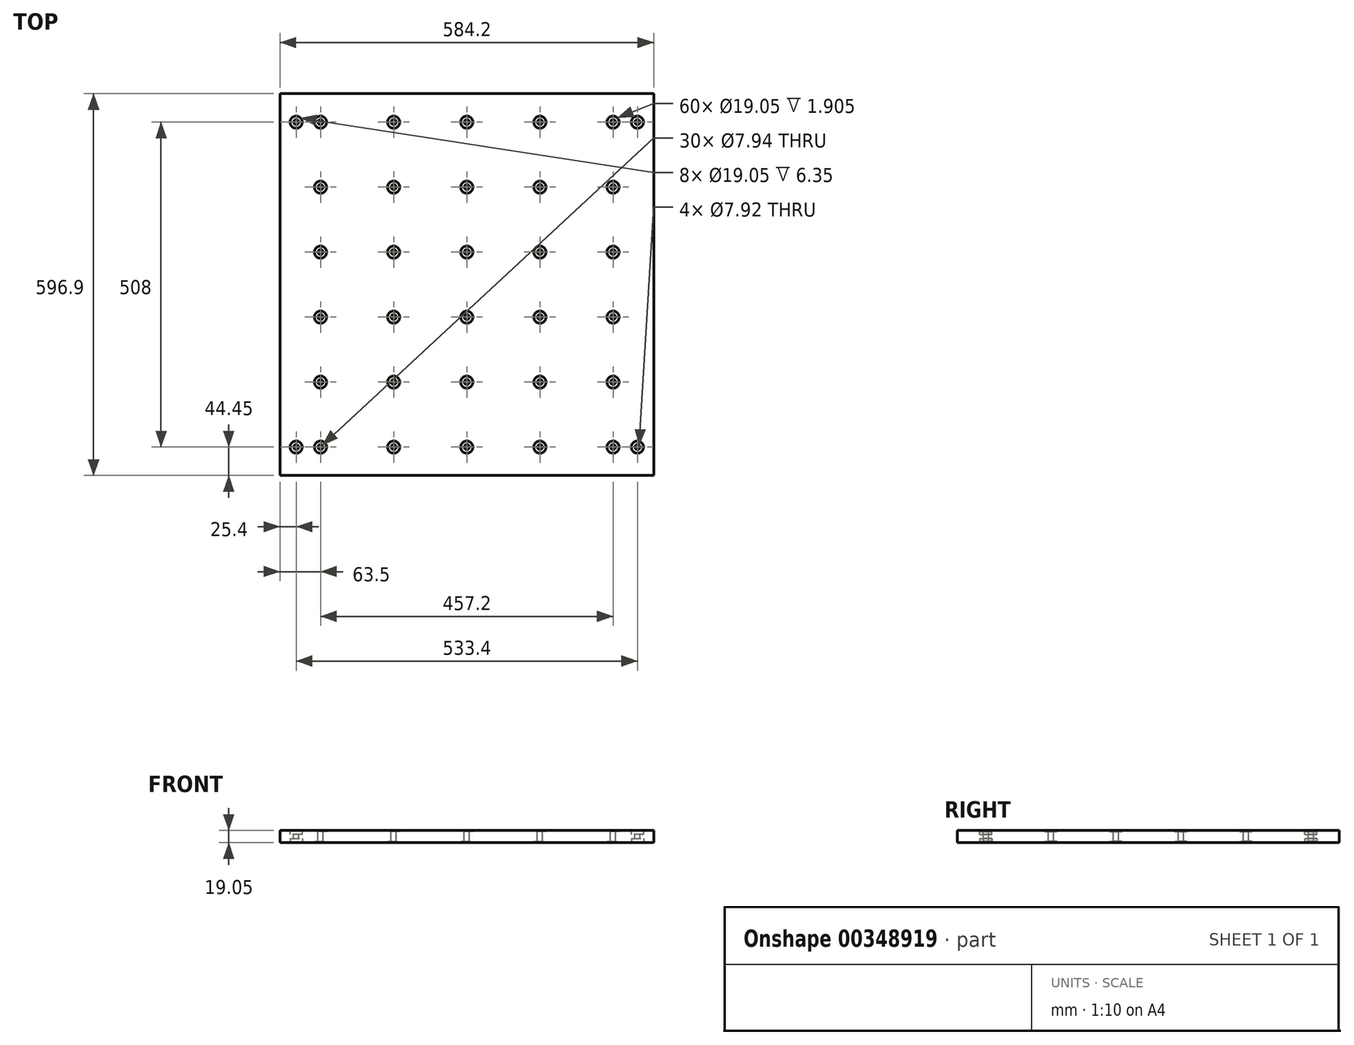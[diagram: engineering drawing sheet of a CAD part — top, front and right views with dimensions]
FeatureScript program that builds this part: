
annotation { "Feature Type Name" : "Feature", "Feature Type Description" : "" }
export const myFeature = defineFeature(function(context is Context, id is Id, definition is map)
    precondition{}
    {
        {
            var Q0;
            Q0=qCreatedBy(makeId("Top.planeOp"),FACE);
            var sketch = newSketch(context, id + "F0", { "sketchPlane" : qUnion([Q0])});
            skLineSegment(sketch, "E0.bottom", {"start": v(0, 0) * mm, "end": v(584.2, 0) * mm});
            skLineSegment(sketch, "E0.top", {"start": v(0, -596.9) * mm, "end": v(584.2, -596.9) * mm});
            skLineSegment(sketch, "E0.left", {"start": v(0, 0) * mm, "end": v(0, -596.9) * mm});
            skLineSegment(sketch, "E0.right", {"start": v(584.2, 0) * mm, "end": v(584.2, -596.9) * mm});
            skSolve(sketch);
        }
        {
            var Q0;
            Q0=qSketchRegion(id+"F0",true);
            extrude(context, id + "F1", {"entities" : qUnion([Q0]), "depth" : 19.05 * mm});
        }
        {
            var Q0;
            Q0=makeQuery(id+"F1.opExtrude","CAP_FACE",FACE,{"disambiguationData":[OSD([sQuery(id+"F0.wireOp",EDGE,"E0.bottom"),sQuery(id+"F0.wireOp",EDGE,"E0.top"),sQuery(id+"F0.wireOp",EDGE,"E0.left"),sQuery(id+"F0.wireOp",EDGE,"E0.right")])],"isStart":false});
            var sketch = newSketch(context, id + "F2", { "sketchPlane" : qUnion([Q0])});
            skCircle(sketch, "E1", {"center": v(25.4, -552.45) * mm, "radius": 9.53 * mm});
            skCircle(sketch, "E2.0.1.0", {"center": v(25.4, -44.45) * mm, "radius": 9.53 * mm});
            skCircle(sketch, "E2.1.0.0", {"center": v(558.8, -552.45) * mm, "radius": 9.53 * mm});
            skCircle(sketch, "E2.1.1.0", {"center": v(558.8, -44.45) * mm, "radius": 9.53 * mm});
            skLineSegment(sketch, "E2.direction1", {"start": v(25.4, -552.45) * mm, "end": v(558.8, -552.45) * mm, "construction": true});
            skLineSegment(sketch, "E2.direction2", {"start": v(25.4, -552.45) * mm, "end": v(25.4, -44.45) * mm, "construction": true});
            skSolve(sketch);
        }
        {
            var Q0;
            Q0=qSketchRegion(id+"F2",true);
            extrude(context, id + "F3", {"entities" : qUnion([Q0]), "operationType" : NewBodyOperationType.REMOVE, "oppositeDirection" : true, "depth" : 6.35 * mm});
        }
        {
            var Q0;
            Q0=makeQuery(id+"F1.opExtrude","CAP_FACE",FACE,{"disambiguationData":[OSD([sQuery(id+"F0.wireOp",EDGE,"E0.bottom"),sQuery(id+"F0.wireOp",EDGE,"E0.top"),sQuery(id+"F0.wireOp",EDGE,"E0.left"),sQuery(id+"F0.wireOp",EDGE,"E0.right")])],"isStart":false});
            var sketch = newSketch(context, id + "F4", { "sketchPlane" : qUnion([Q0])});
            skCircle(sketch, "E3", {"center": v(25.4, -552.45) * mm, "radius": 3.96 * mm});
            skCircle(sketch, "E4.0.1.0", {"center": v(25.4, -44.45) * mm, "radius": 3.96 * mm});
            skCircle(sketch, "E4.1.0.0", {"center": v(558.8, -552.45) * mm, "radius": 3.96 * mm});
            skCircle(sketch, "E4.1.1.0", {"center": v(558.8, -44.45) * mm, "radius": 3.96 * mm});
            skLineSegment(sketch, "E4.direction1", {"start": v(25.4, -552.45) * mm, "end": v(558.8, -552.45) * mm, "construction": true});
            skLineSegment(sketch, "E4.direction2", {"start": v(25.4, -552.45) * mm, "end": v(25.4, -44.45) * mm, "construction": true});
            skSolve(sketch);
        }
        {
            var Q0;
            Q0=qSketchRegion(id+"F4",true);
            extrude(context, id + "F5", {"entities" : qUnion([Q0]), "operationType" : NewBodyOperationType.REMOVE, "endBound" : BoundingType.THROUGH_ALL, "oppositeDirection" : true, "depth" : 25.4 * mm});
        }
        {
            var Q0;
            Q0=makeQuery(id+"F1.opExtrude","CAP_FACE",FACE,{"disambiguationData":[OSD([sQuery(id+"F0.wireOp",EDGE,"E0.bottom"),sQuery(id+"F0.wireOp",EDGE,"E0.top"),sQuery(id+"F0.wireOp",EDGE,"E0.left"),sQuery(id+"F0.wireOp",EDGE,"E0.right")])],"isStart":true});
            var sketch = newSketch(context, id + "F6", { "sketchPlane" : qUnion([Q0])});
            skCircle(sketch, "E5", {"center": v(25.4, 44.45) * mm, "radius": 9.53 * mm});
            skCircle(sketch, "E6.0.1.0", {"center": v(25.4, 552.45) * mm, "radius": 9.53 * mm});
            skCircle(sketch, "E6.1.0.0", {"center": v(558.8, 44.45) * mm, "radius": 9.53 * mm});
            skCircle(sketch, "E6.1.1.0", {"center": v(558.8, 552.45) * mm, "radius": 9.53 * mm});
            skLineSegment(sketch, "E6.direction1", {"start": v(25.4, 44.45) * mm, "end": v(558.8, 44.45) * mm, "construction": true});
            skLineSegment(sketch, "E6.direction2", {"start": v(25.4, 44.45) * mm, "end": v(25.4, 552.45) * mm, "construction": true});
            skSolve(sketch);
        }
        {
            var Q0;
            Q0=qSketchRegion(id+"F6",true);
            extrude(context, id + "F7", {"entities" : qUnion([Q0]), "operationType" : NewBodyOperationType.REMOVE, "oppositeDirection" : true, "depth" : 6.35 * mm});
        }
        {
            var Q0;
            Q0=makeQuery(id+"F1.opExtrude","CAP_FACE",FACE,{"disambiguationData":[OSD([sQuery(id+"F0.wireOp",EDGE,"E0.bottom"),sQuery(id+"F0.wireOp",EDGE,"E0.top"),sQuery(id+"F0.wireOp",EDGE,"E0.left"),sQuery(id+"F0.wireOp",EDGE,"E0.right")])],"isStart":false});
            var sketch = newSketch(context, id + "F8", { "sketchPlane" : qUnion([Q0])});
            skCircle(sketch, "E7", {"center": v(63.5, -552.45) * mm, "radius": 9.53 * mm});
            skCircle(sketch, "E8.0.1.0", {"center": v(63.5, -450.85) * mm, "radius": 9.53 * mm});
            skCircle(sketch, "E8.0.2.0", {"center": v(63.5, -349.25) * mm, "radius": 9.53 * mm});
            skCircle(sketch, "E8.0.3.0", {"center": v(63.5, -247.65) * mm, "radius": 9.53 * mm});
            skCircle(sketch, "E8.0.4.0", {"center": v(63.5, -146.05) * mm, "radius": 9.53 * mm});
            skCircle(sketch, "E8.0.5.0", {"center": v(63.5, -44.45) * mm, "radius": 9.53 * mm});
            skCircle(sketch, "E8.1.0.0", {"center": v(177.8, -552.45) * mm, "radius": 9.53 * mm});
            skCircle(sketch, "E8.1.1.0", {"center": v(177.8, -450.85) * mm, "radius": 9.53 * mm});
            skCircle(sketch, "E8.1.2.0", {"center": v(177.8, -349.25) * mm, "radius": 9.53 * mm});
            skCircle(sketch, "E8.1.3.0", {"center": v(177.8, -247.65) * mm, "radius": 9.53 * mm});
            skCircle(sketch, "E8.1.4.0", {"center": v(177.8, -146.05) * mm, "radius": 9.53 * mm});
            skCircle(sketch, "E8.1.5.0", {"center": v(177.8, -44.45) * mm, "radius": 9.53 * mm});
            skCircle(sketch, "E8.2.0.0", {"center": v(292.1, -552.45) * mm, "radius": 9.53 * mm});
            skCircle(sketch, "E8.2.1.0", {"center": v(292.1, -450.85) * mm, "radius": 9.53 * mm});
            skCircle(sketch, "E8.2.2.0", {"center": v(292.1, -349.25) * mm, "radius": 9.53 * mm});
            skCircle(sketch, "E8.2.3.0", {"center": v(292.1, -247.65) * mm, "radius": 9.53 * mm});
            skCircle(sketch, "E8.2.4.0", {"center": v(292.1, -146.05) * mm, "radius": 9.53 * mm});
            skCircle(sketch, "E8.2.5.0", {"center": v(292.1, -44.45) * mm, "radius": 9.53 * mm});
            skCircle(sketch, "E8.3.0.0", {"center": v(406.4, -552.45) * mm, "radius": 9.53 * mm});
            skCircle(sketch, "E8.3.1.0", {"center": v(406.4, -450.85) * mm, "radius": 9.53 * mm});
            skCircle(sketch, "E8.3.2.0", {"center": v(406.4, -349.25) * mm, "radius": 9.53 * mm});
            skCircle(sketch, "E8.3.3.0", {"center": v(406.4, -247.65) * mm, "radius": 9.53 * mm});
            skCircle(sketch, "E8.3.4.0", {"center": v(406.4, -146.05) * mm, "radius": 9.53 * mm});
            skCircle(sketch, "E8.3.5.0", {"center": v(406.4, -44.45) * mm, "radius": 9.53 * mm});
            skCircle(sketch, "E8.4.0.0", {"center": v(520.7, -552.45) * mm, "radius": 9.53 * mm});
            skCircle(sketch, "E8.4.1.0", {"center": v(520.7, -450.85) * mm, "radius": 9.53 * mm});
            skCircle(sketch, "E8.4.2.0", {"center": v(520.7, -349.25) * mm, "radius": 9.53 * mm});
            skCircle(sketch, "E8.4.3.0", {"center": v(520.7, -247.65) * mm, "radius": 9.53 * mm});
            skCircle(sketch, "E8.4.4.0", {"center": v(520.7, -146.05) * mm, "radius": 9.53 * mm});
            skCircle(sketch, "E8.4.5.0", {"center": v(520.7, -44.45) * mm, "radius": 9.53 * mm});
            skLineSegment(sketch, "E8.direction1", {"start": v(63.5, -552.45) * mm, "end": v(177.8, -552.45) * mm, "construction": true});
            skLineSegment(sketch, "E8.direction2", {"start": v(63.5, -552.45) * mm, "end": v(63.5, -450.85) * mm, "construction": true});
            skSolve(sketch);
        }
        {
            var Q0;
            Q0=qSketchRegion(id+"F8",true);
            extrude(context, id + "F9", {"entities" : qUnion([Q0]), "operationType" : NewBodyOperationType.REMOVE, "oppositeDirection" : true, "depth" : 1.9 * mm});
        }
        {
            var Q0;
            Q0=makeQuery(id+"F1.opExtrude","CAP_FACE",FACE,{"disambiguationData":[OSD([sQuery(id+"F0.wireOp",EDGE,"E0.bottom"),sQuery(id+"F0.wireOp",EDGE,"E0.top"),sQuery(id+"F0.wireOp",EDGE,"E0.left"),sQuery(id+"F0.wireOp",EDGE,"E0.right")])],"isStart":false});
            var sketch = newSketch(context, id + "F10", { "sketchPlane" : qUnion([Q0])});
            skCircle(sketch, "E9", {"center": v(63.5, -552.45) * mm, "radius": 3.97 * mm});
            skCircle(sketch, "E10.0.1.0", {"center": v(63.5, -450.85) * mm, "radius": 3.97 * mm});
            skCircle(sketch, "E10.0.2.0", {"center": v(63.5, -349.25) * mm, "radius": 3.97 * mm});
            skCircle(sketch, "E10.0.3.0", {"center": v(63.5, -247.65) * mm, "radius": 3.97 * mm});
            skCircle(sketch, "E10.0.4.0", {"center": v(63.5, -146.05) * mm, "radius": 3.97 * mm});
            skCircle(sketch, "E10.0.5.0", {"center": v(63.5, -44.45) * mm, "radius": 3.97 * mm});
            skCircle(sketch, "E10.1.0.0", {"center": v(177.8, -552.45) * mm, "radius": 3.97 * mm});
            skCircle(sketch, "E10.1.1.0", {"center": v(177.8, -450.85) * mm, "radius": 3.97 * mm});
            skCircle(sketch, "E10.1.2.0", {"center": v(177.8, -349.25) * mm, "radius": 3.97 * mm});
            skCircle(sketch, "E10.1.3.0", {"center": v(177.8, -247.65) * mm, "radius": 3.97 * mm});
            skCircle(sketch, "E10.1.4.0", {"center": v(177.8, -146.05) * mm, "radius": 3.97 * mm});
            skCircle(sketch, "E10.1.5.0", {"center": v(177.8, -44.45) * mm, "radius": 3.97 * mm});
            skCircle(sketch, "E10.2.0.0", {"center": v(292.1, -552.45) * mm, "radius": 3.97 * mm});
            skCircle(sketch, "E10.2.1.0", {"center": v(292.1, -450.85) * mm, "radius": 3.97 * mm});
            skCircle(sketch, "E10.2.2.0", {"center": v(292.1, -349.25) * mm, "radius": 3.97 * mm});
            skCircle(sketch, "E10.2.3.0", {"center": v(292.1, -247.65) * mm, "radius": 3.97 * mm});
            skCircle(sketch, "E10.2.4.0", {"center": v(292.1, -146.05) * mm, "radius": 3.97 * mm});
            skCircle(sketch, "E10.2.5.0", {"center": v(292.1, -44.45) * mm, "radius": 3.97 * mm});
            skCircle(sketch, "E10.3.0.0", {"center": v(406.4, -552.45) * mm, "radius": 3.97 * mm});
            skCircle(sketch, "E10.3.1.0", {"center": v(406.4, -450.85) * mm, "radius": 3.97 * mm});
            skCircle(sketch, "E10.3.2.0", {"center": v(406.4, -349.25) * mm, "radius": 3.97 * mm});
            skCircle(sketch, "E10.3.3.0", {"center": v(406.4, -247.65) * mm, "radius": 3.97 * mm});
            skCircle(sketch, "E10.3.4.0", {"center": v(406.4, -146.05) * mm, "radius": 3.97 * mm});
            skCircle(sketch, "E10.3.5.0", {"center": v(406.4, -44.45) * mm, "radius": 3.97 * mm});
            skCircle(sketch, "E10.4.0.0", {"center": v(520.7, -552.45) * mm, "radius": 3.97 * mm});
            skCircle(sketch, "E10.4.1.0", {"center": v(520.7, -450.85) * mm, "radius": 3.97 * mm});
            skCircle(sketch, "E10.4.2.0", {"center": v(520.7, -349.25) * mm, "radius": 3.97 * mm});
            skCircle(sketch, "E10.4.3.0", {"center": v(520.7, -247.65) * mm, "radius": 3.97 * mm});
            skCircle(sketch, "E10.4.4.0", {"center": v(520.7, -146.05) * mm, "radius": 3.97 * mm});
            skCircle(sketch, "E10.4.5.0", {"center": v(520.7, -44.45) * mm, "radius": 3.97 * mm});
            skLineSegment(sketch, "E10.direction1", {"start": v(63.5, -552.45) * mm, "end": v(177.8, -552.45) * mm, "construction": true});
            skLineSegment(sketch, "E10.direction2", {"start": v(63.5, -552.45) * mm, "end": v(63.5, -450.85) * mm, "construction": true});
            skSolve(sketch);
        }
        {
            var Q0;
            Q0=qSketchRegion(id+"F10",true);
            extrude(context, id + "F11", {"entities" : qUnion([Q0]), "operationType" : NewBodyOperationType.REMOVE, "endBound" : BoundingType.THROUGH_ALL, "oppositeDirection" : true, "depth" : 25.4 * mm});
        }
        {
            var Q0;
            Q0=makeQuery(id+"F1.opExtrude","CAP_FACE",FACE,{"disambiguationData":[OSD([sQuery(id+"F0.wireOp",EDGE,"E0.bottom"),sQuery(id+"F0.wireOp",EDGE,"E0.top"),sQuery(id+"F0.wireOp",EDGE,"E0.left"),sQuery(id+"F0.wireOp",EDGE,"E0.right")])],"isStart":true});
            var sketch = newSketch(context, id + "F12", { "sketchPlane" : qUnion([Q0])});
            skCircle(sketch, "E11", {"center": v(63.5, 552.45) * mm, "radius": 9.53 * mm});
            skCircle(sketch, "E12.0.1.0", {"center": v(63.5, 450.85) * mm, "radius": 9.53 * mm});
            skCircle(sketch, "E12.0.2.0", {"center": v(63.5, 349.25) * mm, "radius": 9.53 * mm});
            skCircle(sketch, "E12.0.3.0", {"center": v(63.5, 247.65) * mm, "radius": 9.53 * mm});
            skCircle(sketch, "E12.0.4.0", {"center": v(63.5, 146.05) * mm, "radius": 9.53 * mm});
            skCircle(sketch, "E12.0.5.0", {"center": v(63.5, 44.45) * mm, "radius": 9.53 * mm});
            skCircle(sketch, "E12.1.0.0", {"center": v(177.8, 552.45) * mm, "radius": 9.53 * mm});
            skCircle(sketch, "E12.1.1.0", {"center": v(177.8, 450.85) * mm, "radius": 9.53 * mm});
            skCircle(sketch, "E12.1.2.0", {"center": v(177.8, 349.25) * mm, "radius": 9.53 * mm});
            skCircle(sketch, "E12.1.3.0", {"center": v(177.8, 247.65) * mm, "radius": 9.53 * mm});
            skCircle(sketch, "E12.1.4.0", {"center": v(177.8, 146.05) * mm, "radius": 9.53 * mm});
            skCircle(sketch, "E12.1.5.0", {"center": v(177.8, 44.45) * mm, "radius": 9.53 * mm});
            skCircle(sketch, "E12.2.0.0", {"center": v(292.1, 552.45) * mm, "radius": 9.53 * mm});
            skCircle(sketch, "E12.2.1.0", {"center": v(292.1, 450.85) * mm, "radius": 9.53 * mm});
            skCircle(sketch, "E12.2.2.0", {"center": v(292.1, 349.25) * mm, "radius": 9.53 * mm});
            skCircle(sketch, "E12.2.3.0", {"center": v(292.1, 247.65) * mm, "radius": 9.53 * mm});
            skCircle(sketch, "E12.2.4.0", {"center": v(292.1, 146.05) * mm, "radius": 9.53 * mm});
            skCircle(sketch, "E12.2.5.0", {"center": v(292.1, 44.45) * mm, "radius": 9.53 * mm});
            skCircle(sketch, "E12.3.0.0", {"center": v(406.4, 552.45) * mm, "radius": 9.53 * mm});
            skCircle(sketch, "E12.3.1.0", {"center": v(406.4, 450.85) * mm, "radius": 9.53 * mm});
            skCircle(sketch, "E12.3.2.0", {"center": v(406.4, 349.25) * mm, "radius": 9.53 * mm});
            skCircle(sketch, "E12.3.3.0", {"center": v(406.4, 247.65) * mm, "radius": 9.53 * mm});
            skCircle(sketch, "E12.3.4.0", {"center": v(406.4, 146.05) * mm, "radius": 9.53 * mm});
            skCircle(sketch, "E12.3.5.0", {"center": v(406.4, 44.45) * mm, "radius": 9.53 * mm});
            skCircle(sketch, "E12.4.0.0", {"center": v(520.7, 552.45) * mm, "radius": 9.53 * mm});
            skCircle(sketch, "E12.4.1.0", {"center": v(520.7, 450.85) * mm, "radius": 9.53 * mm});
            skCircle(sketch, "E12.4.2.0", {"center": v(520.7, 349.25) * mm, "radius": 9.53 * mm});
            skCircle(sketch, "E12.4.3.0", {"center": v(520.7, 247.65) * mm, "radius": 9.53 * mm});
            skCircle(sketch, "E12.4.4.0", {"center": v(520.7, 146.05) * mm, "radius": 9.53 * mm});
            skCircle(sketch, "E12.4.5.0", {"center": v(520.7, 44.45) * mm, "radius": 9.53 * mm});
            skLineSegment(sketch, "E12.direction1", {"start": v(63.5, 552.45) * mm, "end": v(177.8, 552.45) * mm, "construction": true});
            skLineSegment(sketch, "E12.direction2", {"start": v(63.5, 552.45) * mm, "end": v(63.5, 450.85) * mm, "construction": true});
            skSolve(sketch);
        }
        {
            var Q0;
            Q0=qSketchRegion(id+"F12",true);
            extrude(context, id + "F13", {"entities" : qUnion([Q0]), "operationType" : NewBodyOperationType.REMOVE, "oppositeDirection" : true, "depth" : 1.9 * mm});
        }
    });
